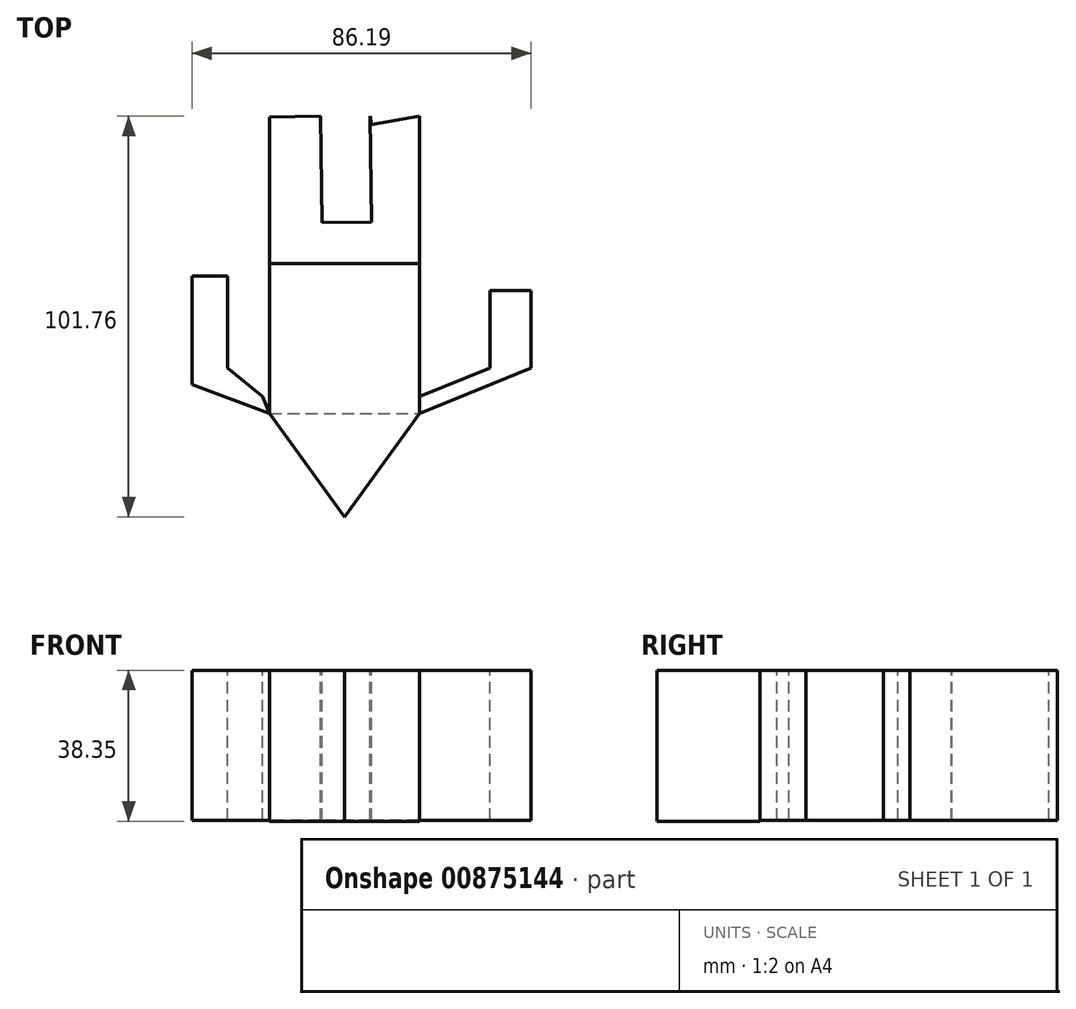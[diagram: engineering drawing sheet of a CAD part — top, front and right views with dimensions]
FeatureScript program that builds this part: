
annotation { "Feature Type Name" : "Feature", "Feature Type Description" : "" }
export const myFeature = defineFeature(function(context is Context, id is Id, definition is map)
    precondition{}
    {
        {
            var Q0;
            Q0=qCreatedBy(makeId("Top.planeOp"),FACE);
            var sketch = newSketch(context, id + "F0", { "sketchPlane" : qUnion([Q0])});
            skLineSegment(sketch, "E0.bottom", {"start": v(-19.05, 19.05) * mm, "end": v(19.05, 19.05) * mm});
            skLineSegment(sketch, "E0.top", {"start": v(-19.05, -19.05) * mm, "end": v(19.05, -19.05) * mm});
            skLineSegment(sketch, "E0.left", {"start": v(-19.05, 19.05) * mm, "end": v(-19.05, -19.05) * mm});
            skLineSegment(sketch, "E0.right", {"start": v(19.05, 19.05) * mm, "end": v(19.05, -19.05) * mm});
            skPoint(sketch, "E0.middle", {"position": v(0, 0) * mm});
            skSolve(sketch);
        }
        {
            var Q0;
            Q0=makeQuery(id+"F0.imprint","IMPRINT",FACE,{"disambiguationData":[TD([[makeQuery(id+"F0.imprint","IMPRINT",EDGE,{"derivedFrom":sQuery(id+"F0.wireOp",EDGE,"E0.bottom")}),-1.0]])]});
            var sketch = newSketch(context, id + "F1", { "sketchPlane" : qUnion([Q0])});
            skSolve(sketch);
        }
        {
            var Q0;
            Q0 = qSketchRegion(id + "F1", true);
            var Q1;
            Q1=makeQuery(id+"F0.imprint","IMPRINT",FACE,{"disambiguationData":[TD([[makeQuery(id+"F0.imprint","IMPRINT",EDGE,{"derivedFrom":sQuery(id+"F0.wireOp",EDGE,"E0.bottom")}),-1.0]])]});
            extrude(context, id + "F2", {"entities" : qUnion([Q0, Q1]), "depth" : 38.1 * mm, "offsetDistance" : 25.4 * mm});
        }
        {
            var Q0;
            Q0=makeQuery(id+"F2.opExtrude","CAP_FACE",FACE,{"disambiguationData":[OSD([sQuery(id+"F0.wireOp",EDGE,"E0.bottom"),sQuery(id+"F0.wireOp",EDGE,"E0.top"),sQuery(id+"F0.wireOp",EDGE,"E0.left"),sQuery(id+"F0.wireOp",EDGE,"E0.right")])],"isStart":false});
            var sketch = newSketch(context, id + "F3", { "sketchPlane" : qUnion([Q0])});
            skLineSegment(sketch, "E1", {"start": v(-19.05, -19.05) * mm, "end": v(-19.05, -45.24) * mm});
            skLineSegment(sketch, "E2", {"start": v(-19.05, -45.24) * mm, "end": v(19.05, -45.24) * mm});
            skLineSegment(sketch, "E3", {"start": v(19.05, -45.24) * mm, "end": v(19.05, -19.05) * mm});
            skLineSegment(sketch, "E4", {"start": v(19.05, -19.05) * mm, "end": v(0, -45.24) * mm});
            skLineSegment(sketch, "E5", {"start": v(0, -45.24) * mm, "end": v(-19.05, -19.05) * mm});
            skSolve(sketch);
        }
        {
            var Q0;
            Q0=makeQuery(id+"F3.imprint","IMPRINT",FACE,{"disambiguationData":[TD([[makeQuery(id+"F3.imprint","IMPRINT",EDGE,{"derivedFrom":sQuery(id+"F3.wireOp",EDGE,"E4")}),-1.0]])]});
            extrude(context, id + "F4", {"entities" : qUnion([Q0]), "operationType" : NewBodyOperationType.ADD, "oppositeDirection" : true, "depth" : 38.35 * mm, "offsetDistance" : 25.4 * mm});
        }
        {
            var Q0;
            {var subQ0=sQuery(id+"F0.wireOp",EDGE,"E0.top");Q0=makeQuery(id+"F4.boolean.opBoolean","MERGE",FACE,{"derivedFrom":[makeQuery(id+"F2.opExtrude","CAP_FACE",FACE,{"disambiguationData":[OSD([sQuery(id+"F0.wireOp",EDGE,"E0.bottom"),subQ0,sQuery(id+"F0.wireOp",EDGE,"E0.left"),sQuery(id+"F0.wireOp",EDGE,"E0.right")])],"isStart":false}),makeQuery(id+"F4.opExtrude","CAP_FACE",FACE,{"disambiguationData":[OSD([subQ0,sQuery(id+"F3.wireOp",EDGE,"E4"),sQuery(id+"F3.wireOp",EDGE,"E5")])],"isStart":true})]});}
            var sketch = newSketch(context, id + "F5", { "sketchPlane" : qUnion([Q0])});
            skLineSegment(sketch, "E6", {"start": v(19.05, -19.05) * mm, "end": v(47.39, -7.38) * mm});
            skLineSegment(sketch, "E7", {"start": v(47.39, -7.38) * mm, "end": v(47.39, 12.22) * mm});
            skLineSegment(sketch, "E8", {"start": v(47.39, 12.22) * mm, "end": v(36.92, 12.22) * mm});
            skLineSegment(sketch, "E9", {"start": v(36.92, 12.22) * mm, "end": v(36.92, -7.38) * mm});
            skLineSegment(sketch, "E10", {"start": v(36.92, -7.38) * mm, "end": v(19.05, -14.74) * mm});
            skLineSegment(sketch, "E11", {"start": v(19.05, -14.74) * mm, "end": v(19.05, -19.05) * mm});
            skLineSegment(sketch, "E12", {"start": v(-19.05, -19.05) * mm, "end": v(-20.82, -14.74) * mm});
            skLineSegment(sketch, "E13", {"start": v(-20.82, -14.74) * mm, "end": v(-19.05, -14.74) * mm});
            skLineSegment(sketch, "E14", {"start": v(-19.05, -14.74) * mm, "end": v(-19.05, -19.05) * mm});
            skLineSegment(sketch, "E15", {"start": v(-19.05, -19.05) * mm, "end": v(-38.8, -11.68) * mm});
            skLineSegment(sketch, "E16", {"start": v(-38.8, -11.68) * mm, "end": v(-38.8, 15.98) * mm});
            skLineSegment(sketch, "E17", {"start": v(-38.8, 15.98) * mm, "end": v(-29.67, 15.98) * mm});
            skLineSegment(sketch, "E18", {"start": v(-29.67, 15.98) * mm, "end": v(-29.67, -7.38) * mm});
            skLineSegment(sketch, "E19", {"start": v(-29.67, -7.38) * mm, "end": v(-20.82, -14.74) * mm});
            skLineSegment(sketch, "E20", {"start": v(19.05, 19.05) * mm, "end": v(19.05, 56.52) * mm});
            skLineSegment(sketch, "E21", {"start": v(19.05, 56.52) * mm, "end": v(6.85, 54.37) * mm});
            skLineSegment(sketch, "E22", {"start": v(6.85, 54.37) * mm, "end": v(6.47, 56.52) * mm});
            skLineSegment(sketch, "E23", {"start": v(6.47, 56.52) * mm, "end": v(19.05, 56.52) * mm});
            skLineSegment(sketch, "E24", {"start": v(6.47, 56.52) * mm, "end": v(6.85, 29.67) * mm});
            skLineSegment(sketch, "E25", {"start": v(6.85, 29.67) * mm, "end": v(-5.75, 29.5) * mm});
            skLineSegment(sketch, "E26", {"start": v(-5.75, 29.5) * mm, "end": v(-6.13, 56.52) * mm});
            skLineSegment(sketch, "E27", {"start": v(-6.13, 56.52) * mm, "end": v(-19.05, 56.34) * mm});
            skLineSegment(sketch, "E28", {"start": v(-19.05, 56.34) * mm, "end": v(-19.05, 19.05) * mm});
            skLineSegment(sketch, "E29", {"start": v(-19.05, 19.05) * mm, "end": v(19.05, 19.05) * mm});
            skSolve(sketch);
        }
        {
            var Q0;
            Q0=makeQuery(id+"F5.imprint","IMPRINT",FACE,{"disambiguationData":[TD([[makeQuery(id+"F5.imprint","IMPRINT",EDGE,{"derivedFrom":sQuery(id+"F5.wireOp",EDGE,"E20")}),1.0]])]});
            var Q1;
            Q1=makeQuery(id+"F5.imprint","IMPRINT",FACE,{"disambiguationData":[TD([[makeQuery(id+"F5.imprint","IMPRINT",EDGE,{"derivedFrom":sQuery(id+"F5.wireOp",EDGE,"E6")}),1.0]])]});
            var Q2;
            Q2=makeQuery(id+"F5.imprint","IMPRINT",FACE,{"disambiguationData":[TD([[makeQuery(id+"F5.imprint","IMPRINT",EDGE,{"derivedFrom":sQuery(id+"F5.wireOp",EDGE,"E12")}),1.0]])]});
            extrude(context, id + "F6", {"entities" : qUnion([Q0, Q1, Q2]), "oppositeDirection" : true, "depth" : 38.1 * mm, "offsetDistance" : 25.4 * mm});
        }
    });
